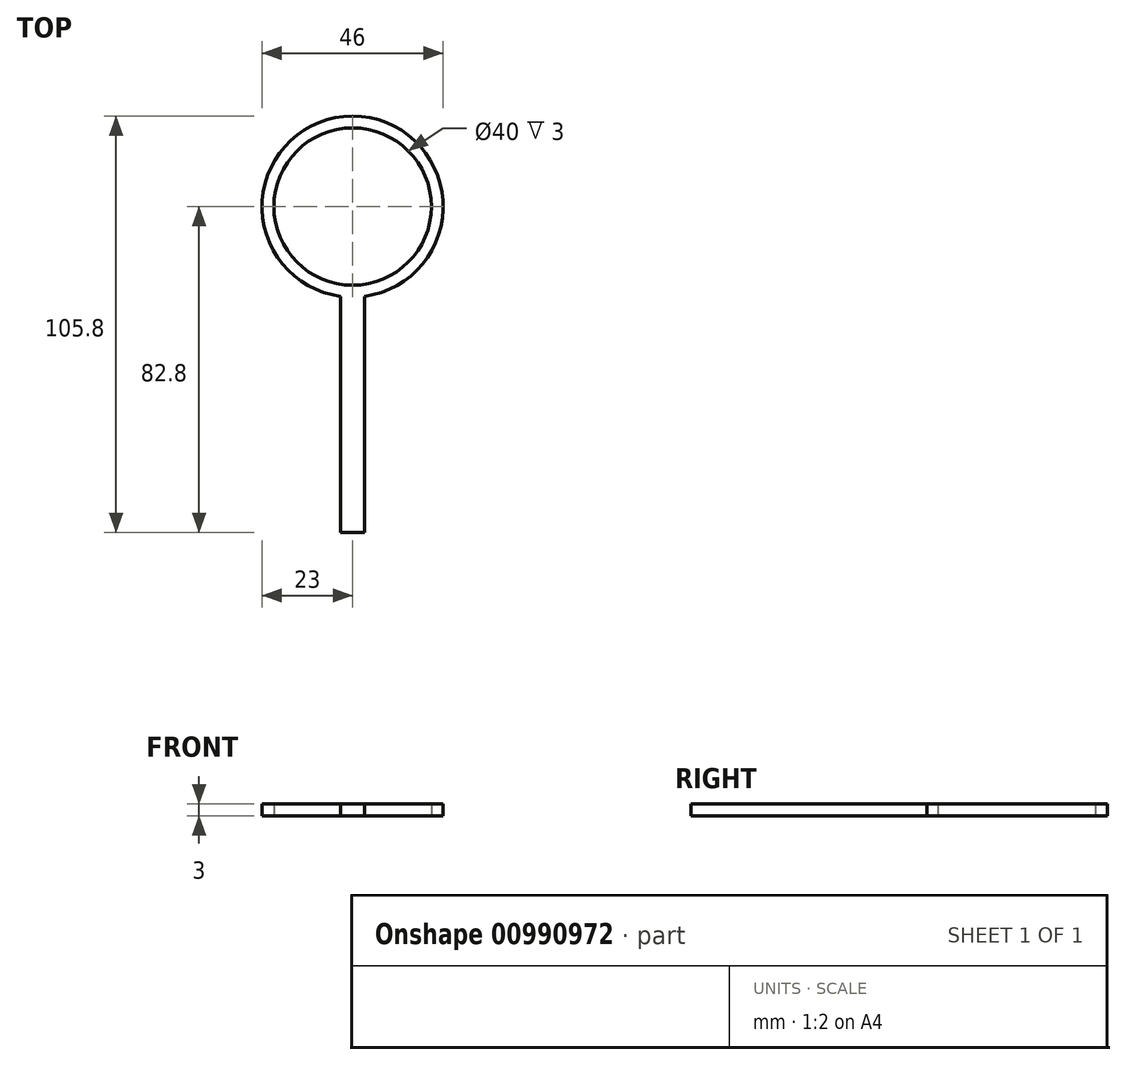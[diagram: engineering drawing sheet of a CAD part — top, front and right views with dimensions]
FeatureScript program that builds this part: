
annotation { "Feature Type Name" : "Feature", "Feature Type Description" : "" }
export const myFeature = defineFeature(function(context is Context, id is Id, definition is map)
    precondition{}
    {
        {
            var Q0;
            Q0=qCreatedBy(makeId("Top.planeOp"),FACE);
            var sketch = newSketch(context, id + "F0", { "sketchPlane" : qUnion([Q0])});
            skCircle(sketch, "E0", {"center": v(0, 0) * mm, "radius": 20 * mm});
            skCircle(sketch, "E1", {"center": v(0, 0) * mm, "radius": 23 * mm});
            skLineSegment(sketch, "E2", {"start": v(-3, -22.8) * mm, "end": v(3, -22.8) * mm, "construction": true});
            skLineSegment(sketch, "E3", {"start": v(-3, -22.8) * mm, "end": v(-3, -82.8) * mm});
            skLineSegment(sketch, "E4", {"start": v(3, -22.8) * mm, "end": v(3, -82.8) * mm});
            skLineSegment(sketch, "E5", {"start": v(-3, -82.8) * mm, "end": v(3, -82.8) * mm});
            skSolve(sketch);
        }
        {
            var Q0;
            {var subQ0=sQuery(id+"F0.wireOp",EDGE,"E3");Q0=makeQuery(id+"F0.imprint","IMPRINT",FACE,{"disambiguationData":[TD([[makeQuery(id+"F0.imprint","IMPRINT",EDGE,{"derivedFrom":subQ0}),1.0]])]});}
            var Q1;
            Q1=makeQuery(id+"F0.imprint","IMPRINT",FACE,{"disambiguationData":[TD([[makeQuery(id+"F0.imprint","IMPRINT",EDGE,{"derivedFrom":sQuery(id+"F0.wireOp",EDGE,"E0")}),-1.0]])]});
            extrude(context, id + "F1", {"entities" : qUnion([Q0, Q1]), "depth" : 3 * mm, "offsetDistance" : 25 * mm});
        }
    });
